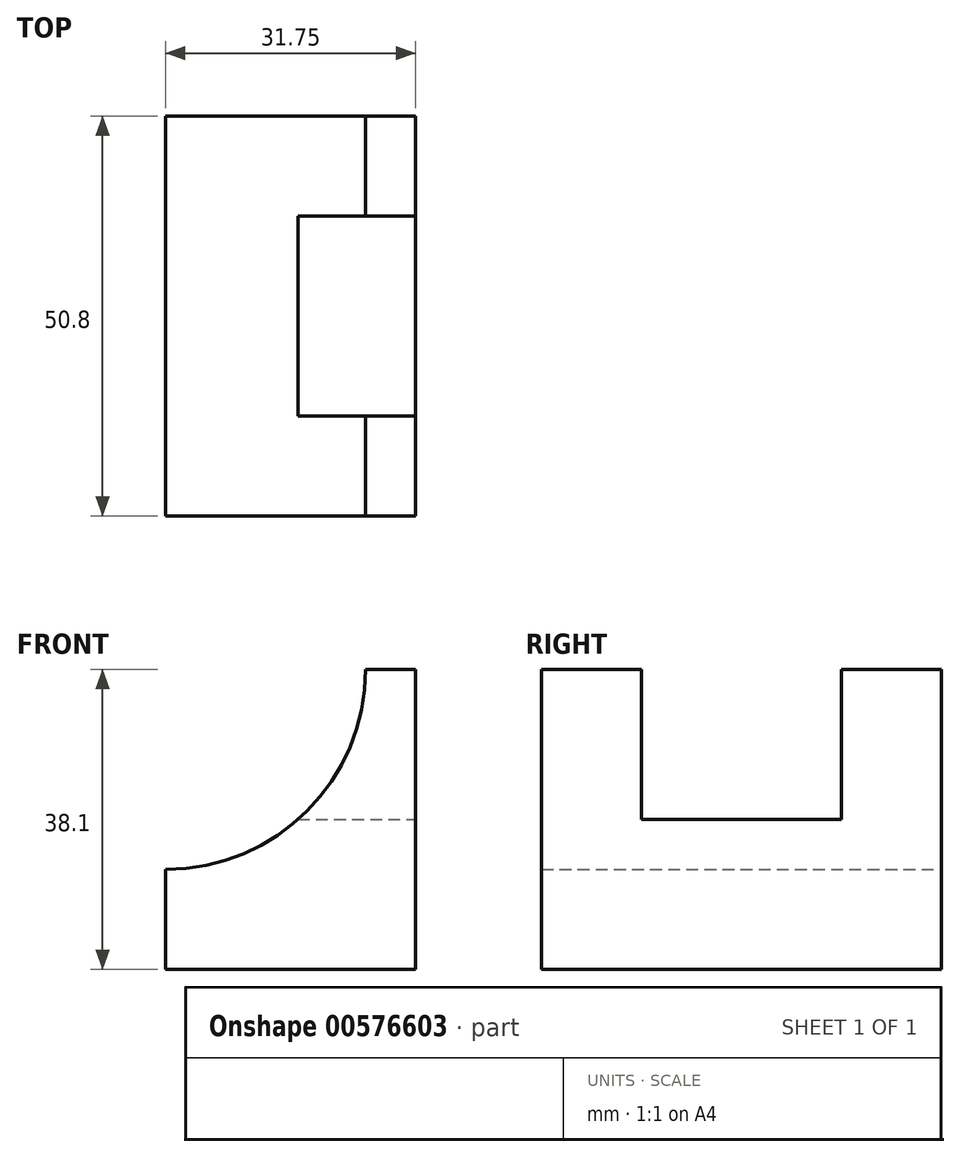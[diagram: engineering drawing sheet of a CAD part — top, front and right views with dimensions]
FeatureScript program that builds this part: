
annotation { "Feature Type Name" : "Feature", "Feature Type Description" : "" }
export const myFeature = defineFeature(function(context is Context, id is Id, definition is map)
    precondition{}
    {
        {
            var Q0;
            Q0=qCreatedBy(makeId("Front.planeOp"),FACE);
            var sketch = newSketch(context, id + "F0", { "sketchPlane" : qUnion([Q0])});
            skLineSegment(sketch, "E0", {"start": v(0, 0) * mm, "end": v(0, 38.1) * mm});
            skLineSegment(sketch, "E1", {"start": v(0, 0) * mm, "end": v(-31.75, 0) * mm});
            skLineSegment(sketch, "E2", {"start": v(-31.75, 12.7) * mm, "end": v(-31.75, 0) * mm});
            skLineSegment(sketch, "E3", {"start": v(0, 38.1) * mm, "end": v(-6.35, 38.1) * mm});
            skArc(sketch, "E4", {"start": v(-31.75, 12.7) * mm, "mid": v(-13.79, 20.14) * mm, "end": v(-6.35, 38.1) * mm});
            skSolve(sketch);
        }
        {
            var Q0;
            Q0=makeQuery(id+"F0.imprint","IMPRINT",FACE,{"disambiguationData":[TD([[makeQuery(id+"F0.imprint","IMPRINT",EDGE,{"derivedFrom":sQuery(id+"F0.wireOp",EDGE,"E0")}),1.0]])]});
            extrude(context, id + "F1", {"entities" : qUnion([Q0]), "depth" : 50.8 * mm, "offsetDistance" : 25.4 * mm});
        }
        {
            var Q0;
            Q0=makeQuery(id+"F1.opExtrude","SWEPT_FACE",FACE,{"disambiguationData":[OSD([sQuery(id+"F0.wireOp",EDGE,"E0")])]});
            var sketch = newSketch(context, id + "F2", { "sketchPlane" : qUnion([Q0])});
            skLineSegment(sketch, "E5", {"start": v(-50.8, 38.1) * mm, "end": v(-38.1, 38.1) * mm});
            skLineSegment(sketch, "E6", {"start": v(0, 38.1) * mm, "end": v(-12.7, 38.1) * mm});
            skLineSegment(sketch, "E7", {"start": v(-38.1, 38.1) * mm, "end": v(-38.1, 19.05) * mm});
            skLineSegment(sketch, "E8", {"start": v(-38.1, 19.05) * mm, "end": v(-12.7, 19.05) * mm});
            skLineSegment(sketch, "E9", {"start": v(-12.7, 38.1) * mm, "end": v(-12.7, 19.05) * mm});
            skSolve(sketch);
        }
        {
            var Q0;
            {var subQ0=sQuery(id+"F2.wireOp",EDGE,"E7");Q0=makeQuery(id+"F2.imprint","IMPRINT",FACE,{"disambiguationData":[TD([[makeQuery(id+"F2.imprint","IMPRINT",EDGE,{"derivedFrom":subQ0}),1.0]])]});}
            extrude(context, id + "F3", {"entities" : qUnion([Q0]), "operationType" : NewBodyOperationType.REMOVE, "oppositeDirection" : true, "depth" : 25.4 * mm, "offsetDistance" : 25.4 * mm});
        }
    });
